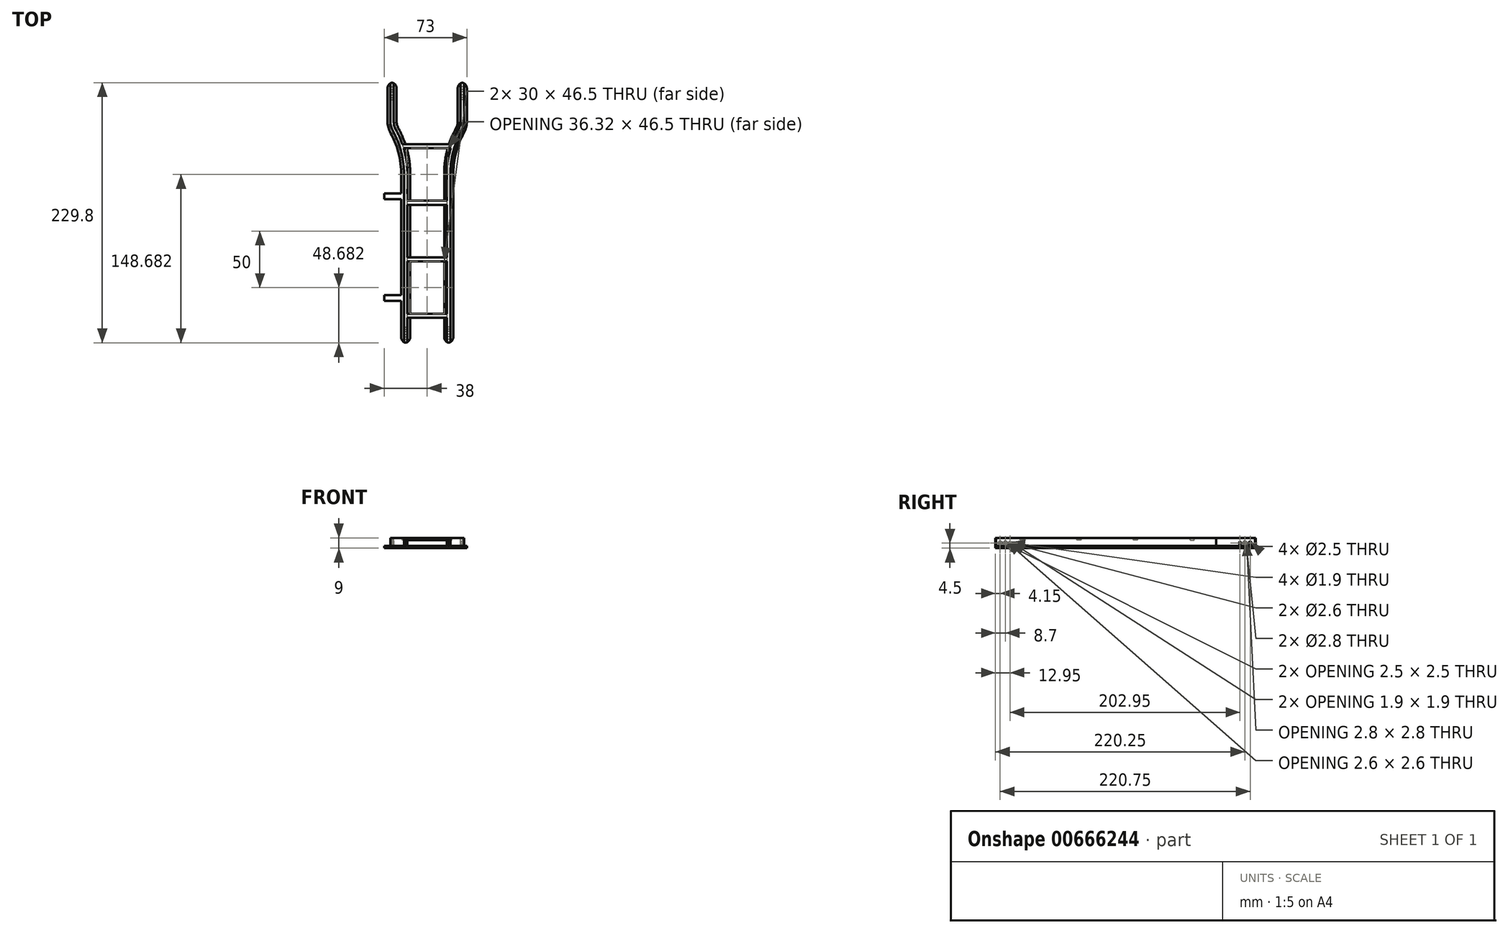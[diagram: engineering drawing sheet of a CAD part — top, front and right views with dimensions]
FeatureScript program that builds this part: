
annotation { "Feature Type Name" : "Feature", "Feature Type Description" : "" }
export const myFeature = defineFeature(function(context is Context, id is Id, definition is map)
    precondition{}
    {
        {
            var Q0;
            Q0=qCreatedBy(makeId("Front.planeOp"),FACE);
            var sketch = newSketch(context, id + "F0", { "sketchPlane" : qUnion([Q0])});
            skLineSegment(sketch, "E0.bottom", {"start": v(-15, 0) * mm, "end": v(-23, 0) * mm});
            skLineSegment(sketch, "E0.top", {"start": v(-15, 9) * mm, "end": v(-23, 9) * mm});
            skLineSegment(sketch, "E0.left", {"start": v(-15, 0) * mm, "end": v(-15, 2) * mm});
            skLineSegment(sketch, "E0.right", {"start": v(-23, 0) * mm, "end": v(-23, 2) * mm});
            skLineSegment(sketch, "E1.bottom", {"start": v(-23, 7) * mm, "end": v(-21, 7) * mm});
            skLineSegment(sketch, "E1.top", {"start": v(-23, 2) * mm, "end": v(-21, 2) * mm});
            skLineSegment(sketch, "E1.right", {"start": v(-20.5, 6.5) * mm, "end": v(-20.5, 2.5) * mm});
            skLineSegment(sketch, "E2.bottom", {"start": v(-17, 7) * mm, "end": v(-15, 7) * mm});
            skLineSegment(sketch, "E2.top", {"start": v(-17, 2) * mm, "end": v(-15, 2) * mm});
            skLineSegment(sketch, "E2.left", {"start": v(-17.5, 6.5) * mm, "end": v(-17.5, 2.5) * mm});
            skLineSegment(sketch, "E3", {"start": v(-19, 9) * mm, "end": v(-19, -4.59) * mm, "construction": true});
            skPoint(sketch, "E3.endSnap0", {"position": v(-19, 0) * mm});
            skLineSegment(sketch, "E4.trimOffspring", {"start": v(-15, 7) * mm, "end": v(-15, 9) * mm});
            skLineSegment(sketch, "E5.trimOffspring", {"start": v(-23, 7) * mm, "end": v(-23, 9) * mm});
            skPoint(sketch, "E6.visualSharp", {"position": v(-20.5, 7) * mm});
            skArc(sketch, "E6.filletArc", {"start": v(-20.5, 6.5) * mm, "mid": v(-20.65, 6.85) * mm, "end": v(-21, 7) * mm});
            skPoint(sketch, "E7.visualSharp", {"position": v(-17.5, 7) * mm});
            skArc(sketch, "E7.filletArc", {"start": v(-17, 7) * mm, "mid": v(-17.35, 6.85) * mm, "end": v(-17.5, 6.5) * mm});
            skPoint(sketch, "E8.visualSharp", {"position": v(-17.5, 2) * mm});
            skArc(sketch, "E8.filletArc", {"start": v(-17.5, 2.5) * mm, "mid": v(-17.35, 2.15) * mm, "end": v(-17, 2) * mm});
            skPoint(sketch, "E9.visualSharp", {"position": v(-20.5, 2) * mm});
            skArc(sketch, "E9.filletArc", {"start": v(-21, 2) * mm, "mid": v(-20.65, 2.15) * mm, "end": v(-20.5, 2.5) * mm});
            skSolve(sketch);
        }
        {
            var Q0;
            Q0=qCreatedBy(makeId("Top.planeOp"),FACE);
            var sketch = newSketch(context, id + "F1", { "sketchPlane" : qUnion([Q0])});
            skLineSegment(sketch, "E10", {"start": v(-35.26, 0) * mm, "end": v(-35.26, 150) * mm});
            skLineSegment(sketch, "E11", {"start": v(-47.26, 230) * mm, "end": v(-47.26, 195) * mm});
            skFitSpline(sketch, "E12", {"points": [v(-35.26, 150) * mm, v(-40.7, 174.86) * mm, v(-47.26, 195) * mm], "startDerivative": vector(-0.38, 53.31) * mm, "endDerivative": vector(-0.87, 58.08) * mm});
            skSolve(sketch);
        }
        {
            var Q0;
            Q0=qSketchRegion(id+"F0",true);
            var Q1;
            Q1=qConstructionFilter(qBodyType(qCreatedBy(id+"F1",EDGE),BodyType.WIRE),ConstructionObject.NO);
            sweep(context, id + "F2", {"profiles" : qUnion([Q0]), "path" : qUnion([Q1])});
        }
        {
            var Q0;
            Q0=qCreatedBy(makeId("Front.planeOp"),FACE);
            var sketch = newSketch(context, id + "F3", { "sketchPlane" : qUnion([Q0])});
            skLineSegment(sketch, "E13.bottom", {"start": v(-17.5, 6.31) * mm, "end": v(-14.7, 6.31) * mm});
            skLineSegment(sketch, "E13.top", {"start": v(-17.5, 10.3) * mm, "end": v(-14.7, 10.3) * mm});
            skLineSegment(sketch, "E13.left", {"start": v(-17.5, 6.31) * mm, "end": v(-17.5, 10.3) * mm});
            skLineSegment(sketch, "E13.right", {"start": v(-14.7, 6.31) * mm, "end": v(-14.7, 10.3) * mm});
            skLineSegment(sketch, "E14.bottom", {"start": v(-20.5, 6.31) * mm, "end": v(-23, 6.31) * mm});
            skLineSegment(sketch, "E14.top", {"start": v(-20.5, 10.3) * mm, "end": v(-23, 10.3) * mm});
            skLineSegment(sketch, "E14.left", {"start": v(-20.5, 6.31) * mm, "end": v(-20.5, 10.3) * mm});
            skLineSegment(sketch, "E14.right", {"start": v(-23, 6.31) * mm, "end": v(-23, 10.3) * mm});
            skSolve(sketch);
        }
        {
            var Q0;
            Q0=makeQuery(id+"F2.opSweep","SWEPT_FACE",FACE,{"disambiguationData":[OSD([sQuery(id+"F0.wireOp",EDGE,"E4.trimOffspring"),sQuery(id+"F1.wireOp",EDGE,"E10")])]});
            var sketch = newSketch(context, id + "F4", { "sketchPlane" : qUnion([Q0])});
            skLineSegment(sketch, "E15.bottom", {"start": v(22.03, 9) * mm, "end": v(25.53, 9) * mm});
            skLineSegment(sketch, "E15.top", {"start": v(22.03, 7) * mm, "end": v(25.53, 7) * mm});
            skLineSegment(sketch, "E15.left", {"start": v(22.03, 9) * mm, "end": v(22.03, 7) * mm});
            skLineSegment(sketch, "E15.right", {"start": v(25.53, 9) * mm, "end": v(25.53, 7) * mm});
            skLineSegment(sketch, "E16.0.1.0", {"start": v(22.03, 2) * mm, "end": v(22.03, 0) * mm});
            skLineSegment(sketch, "E16.0.1.1", {"start": v(22.03, 0) * mm, "end": v(25.53, 0) * mm});
            skLineSegment(sketch, "E16.0.1.2", {"start": v(22.03, 2) * mm, "end": v(25.53, 2) * mm});
            skLineSegment(sketch, "E16.0.1.3", {"start": v(25.53, 2) * mm, "end": v(25.53, 0) * mm});
            skLineSegment(sketch, "E16.1.0.0", {"start": v(72.03, 9) * mm, "end": v(72.03, 7) * mm});
            skLineSegment(sketch, "E16.1.0.1", {"start": v(72.03, 7) * mm, "end": v(75.53, 7) * mm});
            skLineSegment(sketch, "E16.1.0.2", {"start": v(72.03, 9) * mm, "end": v(75.53, 9) * mm});
            skLineSegment(sketch, "E16.1.0.3", {"start": v(75.53, 9) * mm, "end": v(75.53, 7) * mm});
            skLineSegment(sketch, "E16.1.1.0", {"start": v(72.03, 2) * mm, "end": v(72.03, 0) * mm});
            skLineSegment(sketch, "E16.1.1.1", {"start": v(72.03, 0) * mm, "end": v(75.53, 0) * mm});
            skLineSegment(sketch, "E16.1.1.2", {"start": v(72.03, 2) * mm, "end": v(75.53, 2) * mm});
            skLineSegment(sketch, "E16.1.1.3", {"start": v(75.53, 2) * mm, "end": v(75.53, 0) * mm});
            skLineSegment(sketch, "E16.2.0.0", {"start": v(122.03, 9) * mm, "end": v(122.03, 7) * mm});
            skLineSegment(sketch, "E16.2.0.1", {"start": v(122.03, 7) * mm, "end": v(125.53, 7) * mm});
            skLineSegment(sketch, "E16.2.0.2", {"start": v(122.03, 9) * mm, "end": v(125.53, 9) * mm});
            skLineSegment(sketch, "E16.2.0.3", {"start": v(125.53, 9) * mm, "end": v(125.53, 7) * mm});
            skLineSegment(sketch, "E16.2.1.0", {"start": v(122.03, 2) * mm, "end": v(122.03, 0) * mm});
            skLineSegment(sketch, "E16.2.1.1", {"start": v(122.03, 0) * mm, "end": v(125.53, 0) * mm});
            skLineSegment(sketch, "E16.2.1.2", {"start": v(122.03, 2) * mm, "end": v(125.53, 2) * mm});
            skLineSegment(sketch, "E16.2.1.3", {"start": v(125.53, 2) * mm, "end": v(125.53, 0) * mm});
            skLineSegment(sketch, "E16.3.0.0", {"start": v(172.03, 9) * mm, "end": v(172.03, 7) * mm});
            skLineSegment(sketch, "E16.3.0.1", {"start": v(172.03, 7) * mm, "end": v(175.53, 7) * mm});
            skLineSegment(sketch, "E16.3.0.2", {"start": v(172.03, 9) * mm, "end": v(175.53, 9) * mm});
            skLineSegment(sketch, "E16.3.0.3", {"start": v(175.53, 9) * mm, "end": v(175.53, 7) * mm});
            skLineSegment(sketch, "E16.3.1.0", {"start": v(172.03, 2) * mm, "end": v(172.03, 0) * mm});
            skLineSegment(sketch, "E16.3.1.1", {"start": v(172.03, 0) * mm, "end": v(175.53, 0) * mm});
            skLineSegment(sketch, "E16.3.1.2", {"start": v(172.03, 2) * mm, "end": v(175.53, 2) * mm});
            skLineSegment(sketch, "E16.3.1.3", {"start": v(175.53, 2) * mm, "end": v(175.53, 0) * mm});
            skLineSegment(sketch, "E16.direction1", {"start": v(22.03, 7) * mm, "end": v(72.03, 7) * mm, "construction": true});
            skLineSegment(sketch, "E16.direction2", {"start": v(22.03, 7) * mm, "end": v(22.03, 0) * mm, "construction": true});
            skSolve(sketch);
        }
        {
            var Q0;
            Q0=qSketchRegion(id+"F4",true);
            extrude(context, id + "F5", {"entities" : qUnion([Q0]), "operationType" : NewBodyOperationType.ADD, "depth" : 15 * mm});
        }
        {
            var Q0;
            Q0=makeQuery(id+"F5.opExtrude","CAP_FACE",FACE,{"disambiguationData":[OSD([sQuery(id+"F4.wireOp",EDGE,"E16.3.0.0"),sQuery(id+"F4.wireOp",EDGE,"E16.3.0.1"),sQuery(id+"F4.wireOp",EDGE,"E16.3.0.2"),sQuery(id+"F4.wireOp",EDGE,"E16.3.0.3")])],"isStart":true});
            var sketch = newSketch(context, id + "F6", { "sketchPlane" : qUnion([Q0])});
            skLineSegment(sketch, "E17.0", {"start": v(-172.03, 7) * mm, "end": v(-175.53, 7) * mm});
            skLineSegment(sketch, "E18.0.0", {"start": v(-175.53, 9) * mm, "end": v(-175.53, 7) * mm});
            skLineSegment(sketch, "E18.0.1", {"start": v(-175.53, 7) * mm, "end": v(-172.03, 7) * mm});
            skLineSegment(sketch, "E18.0.2", {"start": v(-172.03, 7) * mm, "end": v(-172.03, 9) * mm});
            skLineSegment(sketch, "E18.0.3", {"start": v(-172.03, 9) * mm, "end": v(-175.53, 9) * mm});
            skLineSegment(sketch, "E19.0.0", {"start": v(-175.53, 2) * mm, "end": v(-175.53, 0) * mm});
            skLineSegment(sketch, "E19.0.1", {"start": v(-175.53, 0) * mm, "end": v(-172.03, 0) * mm});
            skLineSegment(sketch, "E19.0.2", {"start": v(-172.03, 0) * mm, "end": v(-172.03, 2) * mm});
            skLineSegment(sketch, "E19.0.3", {"start": v(-172.03, 2) * mm, "end": v(-175.53, 2) * mm});
            skSolve(sketch);
        }
        {
            var Q0;
            Q0=qSketchRegion(id+"F6",true);
            extrude(context, id + "F7", {"entities" : qUnion([Q0]), "operationType" : NewBodyOperationType.ADD, "endBound" : BoundingType.UP_TO_NEXT, "depth" : 25 * mm});
        }
        {
            var Q0;
            Q0=qSketchRegion(id+"F3",true);
            var Q1;
            Q1=qConstructionFilter(qBodyType(qCreatedBy(id+"F1",EDGE),BodyType.WIRE),ConstructionObject.NO);
            sweep(context, id + "F8", {"operationType" : NewBodyOperationType.REMOVE, "profiles" : qUnion([Q0]), "path" : qUnion([Q1])});
        }
        {
            var Q0;
            Q0=qCreatedBy(makeId("Right.planeOp"),FACE);
            var sketch = newSketch(context, id + "F9", { "sketchPlane" : qUnion([Q0])});
            skLineSegment(sketch, "E20.0.0", {"start": v(25.53, 7) * mm, "end": v(25.53, 9) * mm});
            skLineSegment(sketch, "E20.0.1", {"start": v(25.53, 9) * mm, "end": v(22.03, 9) * mm});
            skLineSegment(sketch, "E20.0.2", {"start": v(22.03, 9) * mm, "end": v(22.03, 7) * mm});
            skLineSegment(sketch, "E20.0.3", {"start": v(22.03, 7) * mm, "end": v(25.53, 7) * mm});
            skLineSegment(sketch, "E21.0.0", {"start": v(75.53, 7) * mm, "end": v(75.53, 9) * mm});
            skLineSegment(sketch, "E21.0.1", {"start": v(75.53, 9) * mm, "end": v(72.03, 9) * mm});
            skLineSegment(sketch, "E21.0.2", {"start": v(72.03, 9) * mm, "end": v(72.03, 7) * mm});
            skLineSegment(sketch, "E21.0.3", {"start": v(72.03, 7) * mm, "end": v(75.53, 7) * mm});
            skLineSegment(sketch, "E22.0.0", {"start": v(175.53, 7) * mm, "end": v(175.53, 9) * mm});
            skLineSegment(sketch, "E22.0.1", {"start": v(175.53, 9) * mm, "end": v(172.03, 9) * mm});
            skLineSegment(sketch, "E22.0.2", {"start": v(172.03, 9) * mm, "end": v(172.03, 7) * mm});
            skLineSegment(sketch, "E22.0.3", {"start": v(172.03, 7) * mm, "end": v(175.53, 7) * mm});
            skLineSegment(sketch, "E23.0.0", {"start": v(125.53, 7) * mm, "end": v(125.53, 9) * mm});
            skLineSegment(sketch, "E23.0.1", {"start": v(125.53, 9) * mm, "end": v(122.03, 9) * mm});
            skLineSegment(sketch, "E23.0.2", {"start": v(122.03, 9) * mm, "end": v(122.03, 7) * mm});
            skLineSegment(sketch, "E23.0.3", {"start": v(122.03, 7) * mm, "end": v(125.53, 7) * mm});
            skSolve(sketch);
        }
        {
            var Q0;
            Q0=qSketchRegion(id+"F9",true);
            var Q1;
            Q1=makeQuery(id+"F8.boolean.opBoolean","SPLIT",BODY,{"disambiguationData":[OD(0.0)],"derivedFrom":makeQuery(id+"F2.opSweep","SWEPT_BODY",BODY,{"disambiguationData":[OSD([sQuery(id+"F0.wireOp",EDGE,"E0.bottom"),sQuery(id+"F0.wireOp",EDGE,"E0.top"),sQuery(id+"F0.wireOp",EDGE,"E0.left"),sQuery(id+"F0.wireOp",EDGE,"E0.right"),sQuery(id+"F0.wireOp",EDGE,"E1.bottom"),sQuery(id+"F0.wireOp",EDGE,"E1.top"),sQuery(id+"F0.wireOp",EDGE,"E1.right"),sQuery(id+"F0.wireOp",EDGE,"E2.bottom"),sQuery(id+"F0.wireOp",EDGE,"E2.top"),sQuery(id+"F0.wireOp",EDGE,"E2.left"),sQuery(id+"F0.wireOp",EDGE,"E4.trimOffspring"),sQuery(id+"F0.wireOp",EDGE,"E5.trimOffspring"),sQuery(id+"F0.wireOp",EDGE,"E6.filletArc"),sQuery(id+"F0.wireOp",EDGE,"E7.filletArc"),sQuery(id+"F0.wireOp",EDGE,"E8.filletArc"),sQuery(id+"F0.wireOp",EDGE,"E9.filletArc"),sQuery(id+"F1.wireOp",EDGE,"E11")])]})});
            extrude(context, id + "F10", {"entities" : qUnion([Q0]), "operationType" : NewBodyOperationType.ADD, "endBound" : BoundingType.UP_TO_BODY, "oppositeDirection" : true, "depth" : 25 * mm, "endBoundEntityBody" : qUnion([Q1]), "offsetDistance" : 25 * mm});
        }
        {
            var Q0;
            {var subQ0=sQuery(id+"F1.wireOp",EDGE,"E10");Q0=makeQuery(id+"F8.boolean.opBoolean","MERGE",FACE,{"derivedFrom":[makeQuery(id+"F2.opSweep","SWEPT_FACE",FACE,{"disambiguationData":[OSD([sQuery(id+"F0.wireOp",EDGE,"E2.left"),subQ0])]}),makeQuery(id+"F8.opSweep","SWEPT_FACE",FACE,{"disambiguationData":[OSD([subQ0,sQuery(id+"F3.wireOp",EDGE,"E13.left")])]})]});}
            var sketch = newSketch(context, id + "F11", { "sketchPlane" : qUnion([Q0])});
            skCircle(sketch, "E24", {"center": v(4.25, 4.5) * mm, "radius": 1.25 * mm});
            skCircle(sketch, "E25", {"center": v(8.8, 4.5) * mm, "radius": 1.3 * mm});
            skCircle(sketch, "E26", {"center": v(225, 4.5) * mm, "radius": 1.25 * mm});
            skCircle(sketch, "E27", {"center": v(220.35, 4.5) * mm, "radius": 1.4 * mm});
            skCircle(sketch, "E28", {"center": v(13.05, 4.5) * mm, "radius": 0.95 * mm});
            skCircle(sketch, "E29", {"center": v(216, 4.5) * mm, "radius": 0.95 * mm});
            skSolve(sketch);
        }
        {
            var Q0;
            Q0=qSketchRegion(id+"F11",true);
            extrude(context, id + "F12", {"entities" : qUnion([Q0]), "operationType" : NewBodyOperationType.REMOVE, "endBound" : BoundingType.THROUGH_ALL, "oppositeDirection" : true, "depth" : 25 * mm, "offsetDistance" : 25 * mm});
        }
        {
            var Q0;
            Q0=makeQuery(id+"F2.opSweep","CAP_EDGE",EDGE,{"disambiguationData":[OSD([sQuery(id+"F0.wireOp",EDGE,"E0.left"),sQuery(id+"F1.wireOp",VERTEX,"E10.start")])],"isStart":true});
            var Q1;
            Q1=makeQuery(id+"F2.opSweep","CAP_EDGE",EDGE,{"disambiguationData":[OSD([sQuery(id+"F0.wireOp",EDGE,"E0.right"),sQuery(id+"F1.wireOp",VERTEX,"E10.start")])],"isStart":true});
            var Q2;
            Q2=makeQuery(id+"F2.opSweep","CAP_EDGE",EDGE,{"disambiguationData":[OSD([sQuery(id+"F0.wireOp",EDGE,"E0.right"),sQuery(id+"F1.wireOp",VERTEX,"E11.start")])],"isStart":false});
            var Q3;
            Q3=makeQuery(id+"F2.opSweep","CAP_EDGE",EDGE,{"disambiguationData":[OSD([sQuery(id+"F0.wireOp",EDGE,"E0.left"),sQuery(id+"F1.wireOp",VERTEX,"E11.start")])],"isStart":false});
            fillet(context, id + "F13", {"entities" : qUnion([Q0, Q1, Q2, Q3]), "radius" : 5 * mm, "tangentPropagation" : true, "allowEdgeOverflow" : false});
        }
        {
            var Q0;
            Q0=makeQuery(id+"F8.boolean.opBoolean","SPLIT",BODY,{"disambiguationData":[OD(0.0)],"derivedFrom":makeQuery(id+"F2.opSweep","SWEPT_BODY",BODY,{"disambiguationData":[OSD([sQuery(id+"F0.wireOp",EDGE,"E0.bottom"),sQuery(id+"F0.wireOp",EDGE,"E0.top"),sQuery(id+"F0.wireOp",EDGE,"E0.left"),sQuery(id+"F0.wireOp",EDGE,"E0.right"),sQuery(id+"F0.wireOp",EDGE,"E1.bottom"),sQuery(id+"F0.wireOp",EDGE,"E1.top"),sQuery(id+"F0.wireOp",EDGE,"E1.right"),sQuery(id+"F0.wireOp",EDGE,"E2.bottom"),sQuery(id+"F0.wireOp",EDGE,"E2.top"),sQuery(id+"F0.wireOp",EDGE,"E2.left"),sQuery(id+"F0.wireOp",EDGE,"E4.trimOffspring"),sQuery(id+"F0.wireOp",EDGE,"E5.trimOffspring"),sQuery(id+"F0.wireOp",EDGE,"E6.filletArc"),sQuery(id+"F0.wireOp",EDGE,"E7.filletArc"),sQuery(id+"F0.wireOp",EDGE,"E8.filletArc"),sQuery(id+"F0.wireOp",EDGE,"E9.filletArc"),sQuery(id+"F1.wireOp",EDGE,"E11")])]})});
            var Q1;
            Q1=makeQuery(id+"F5.opExtrude","CAP_FACE",FACE,{"disambiguationData":[OSD([sQuery(id+"F4.wireOp",EDGE,"E15.bottom"),sQuery(id+"F4.wireOp",EDGE,"E15.top"),sQuery(id+"F4.wireOp",EDGE,"E15.left"),sQuery(id+"F4.wireOp",EDGE,"E15.right")])],"isStart":false});
            mirror(context, id + "F14", {"operationType" : NewBodyOperationType.ADD, "entities" : qUnion([Q0]), "mirrorPlane" : qUnion([Q1])});
        }
        {
            var Q0;
            Q0=makeQuery(id+"F2.opSweep","SWEPT_FACE",FACE,{"disambiguationData":[OSD([sQuery(id+"F0.wireOp",EDGE,"E0.right"),sQuery(id+"F1.wireOp",EDGE,"E10")])]});
            var sketch = newSketch(context, id + "F15", { "sketchPlane" : qUnion([Q0])});
            skLineSegment(sketch, "E30.bottom", {"start": v(-37.1, 2) * mm, "end": v(-42.1, 2) * mm});
            skLineSegment(sketch, "E30.top", {"start": v(-37.1, 0) * mm, "end": v(-42.1, 0) * mm});
            skLineSegment(sketch, "E30.left", {"start": v(-37.1, 2) * mm, "end": v(-37.1, 0) * mm});
            skLineSegment(sketch, "E30.right", {"start": v(-42.1, 2) * mm, "end": v(-42.1, 0) * mm});
            skLineSegment(sketch, "E31.bottom", {"start": v(-132.1, 2) * mm, "end": v(-127.1, 2) * mm});
            skLineSegment(sketch, "E31.top", {"start": v(-132.1, 0) * mm, "end": v(-127.1, 0) * mm});
            skLineSegment(sketch, "E31.left", {"start": v(-132.1, 2) * mm, "end": v(-132.1, 0) * mm});
            skLineSegment(sketch, "E31.right", {"start": v(-127.1, 2) * mm, "end": v(-127.1, 0) * mm});
            skSolve(sketch);
        }
        {
            var Q0;
            Q0=qSketchRegion(id+"F15",true);
            extrude(context, id + "F16", {"entities" : qUnion([Q0]), "operationType" : NewBodyOperationType.ADD, "depth" : 15 * mm, "offsetDistance" : 25 * mm});
        }
    });
